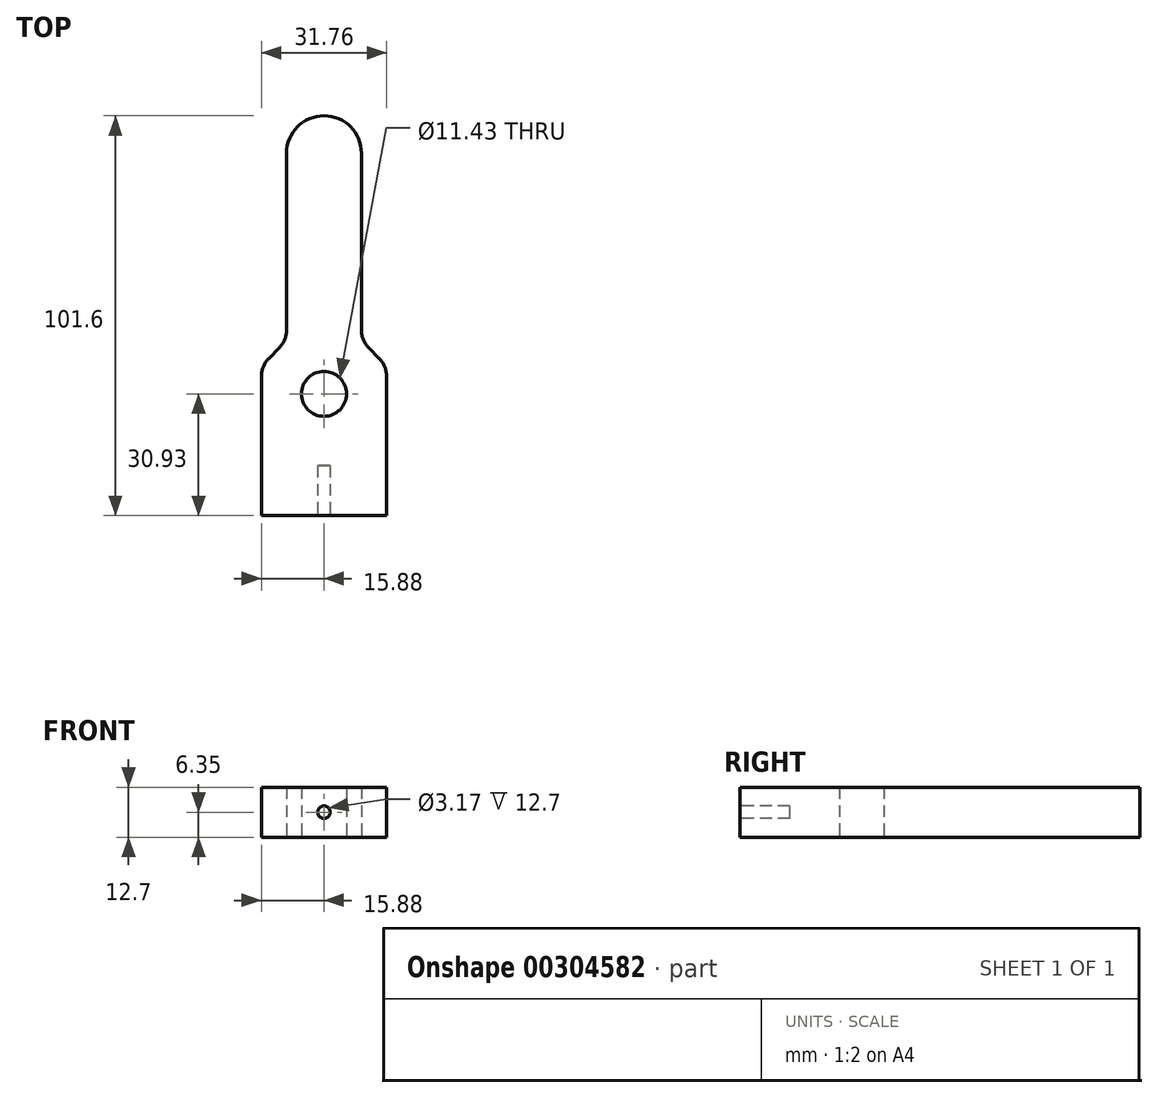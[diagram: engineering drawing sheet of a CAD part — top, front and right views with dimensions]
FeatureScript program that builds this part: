
annotation { "Feature Type Name" : "Feature", "Feature Type Description" : "" }
export const myFeature = defineFeature(function(context is Context, id is Id, definition is map)
    precondition{}
    {
        {
            var Q0;
            Q0=qCreatedBy(makeId("Top.planeOp"),FACE);
            var sketch = newSketch(context, id + "F0", { "sketchPlane" : qUnion([Q0])});
            skLineSegment(sketch, "E0.bottom", {"start": v(-15.87, 7.17) * mm, "end": v(15.88, 7.17) * mm, "construction": true});
            skLineSegment(sketch, "E0.top", {"start": v(-15.87, -30.93) * mm, "end": v(15.87, -30.93) * mm});
            skLineSegment(sketch, "E0.left", {"start": v(-15.87, 4.54) * mm, "end": v(-15.88, -30.93) * mm});
            skLineSegment(sketch, "E0.right", {"start": v(15.88, 4.54) * mm, "end": v(15.87, -30.93) * mm});
            skPoint(sketch, "E0.middle", {"position": v(0, -11.88) * mm});
            skLineSegment(sketch, "E1", {"start": v(0, 7.17) * mm, "end": v(0, 38.92) * mm, "construction": true});
            skPoint(sketch, "E1.endSnap0", {"position": v(0, 7.17) * mm});
            skLineSegment(sketch, "E2.bottom", {"start": v(-9.52, 7.17) * mm, "end": v(9.53, 7.17) * mm, "construction": true});
            skLineSegment(sketch, "E2.top", {"start": v(0, 70.67) * mm, "end": v(0, 70.67) * mm});
            skLineSegment(sketch, "E2.left", {"start": v(-9.52, 16.15) * mm, "end": v(-9.52, 61.14) * mm});
            skLineSegment(sketch, "E2.right", {"start": v(9.53, 16.15) * mm, "end": v(9.53, 61.14) * mm});
            skPoint(sketch, "E2.middle", {"position": v(0, 38.92) * mm});
            skPoint(sketch, "E3.visualSharp", {"position": v(-9.52, 70.67) * mm});
            skArc(sketch, "E3.filletArc", {"start": v(0, 70.67) * mm, "mid": v(-6.74, 67.88) * mm, "end": v(-9.52, 61.14) * mm});
            skPoint(sketch, "E4.visualSharp", {"position": v(9.53, 70.67) * mm});
            skArc(sketch, "E4.filletArc", {"start": v(9.53, 61.14) * mm, "mid": v(6.74, 67.88) * mm, "end": v(0, 70.67) * mm});
            skLineSegment(sketch, "E5", {"start": v(-9.52, 7.17) * mm, "end": v(-9.52, 13.52) * mm, "construction": true});
            skLineSegment(sketch, "E6", {"start": v(-14.02, 9.03) * mm, "end": v(-11.38, 11.66) * mm});
            skLineSegment(sketch, "E7", {"start": v(-9.52, 13.52) * mm, "end": v(9.53, 13.52) * mm, "construction": true});
            skLineSegment(sketch, "E8", {"start": v(11.38, 11.66) * mm, "end": v(14.02, 9.03) * mm});
            skArc(sketch, "E9.filletArc", {"start": v(-11.38, 11.66) * mm, "mid": v(-10, 13.72) * mm, "end": v(-9.52, 16.15) * mm});
            skPoint(sketch, "E10.visualSharp", {"position": v(-15.87, 7.17) * mm});
            skArc(sketch, "E10.filletArc", {"start": v(-14.02, 9.03) * mm, "mid": v(-15.4, 6.97) * mm, "end": v(-15.88, 4.54) * mm});
            skArc(sketch, "E11.filletArc", {"start": v(9.53, 16.15) * mm, "mid": v(10, 13.72) * mm, "end": v(11.38, 11.66) * mm});
            skPoint(sketch, "E12.visualSharp", {"position": v(15.88, 7.17) * mm});
            skArc(sketch, "E12.filletArc", {"start": v(15.88, 4.54) * mm, "mid": v(15.4, 6.97) * mm, "end": v(14.02, 9.03) * mm});
            skLineSegment(sketch, "E13", {"start": v(0, -30.93) * mm, "end": v(0, -1.09) * mm});
            skCircle(sketch, "E14", {"center": v(0, 0) * mm, "radius": 5.72 * mm});
            skSolve(sketch);
        }
        {
            var Q0;
            Q0 = qSketchRegion(id + "F0", true);
            extrude(context, id + "F1", {"entities" : qUnion([Q0]), "endBound" : BoundingType.SYMMETRIC, "depth" : 12.7 * mm});
        }
        {
            var Q0;
            Q0=makeQuery(id+"F1.opExtrude","SWEPT_FACE",FACE,{"disambiguationData":[OSD([sQuery(id+"F0.wireOp",EDGE,"E0.top")])]});
            var sketch = newSketch(context, id + "F2", { "sketchPlane" : qUnion([Q0])});
            skCircle(sketch, "E15", {"center": v(0, 0) * mm, "radius": 1.59 * mm});
            skSolve(sketch);
        }
        {
            var Q0;
            Q0 = qSketchRegion(id + "F2", true);
            extrude(context, id + "F3", {"entities" : qUnion([Q0]), "operationType" : NewBodyOperationType.REMOVE, "oppositeDirection" : true, "depth" : 12.7 * mm});
        }
    });
